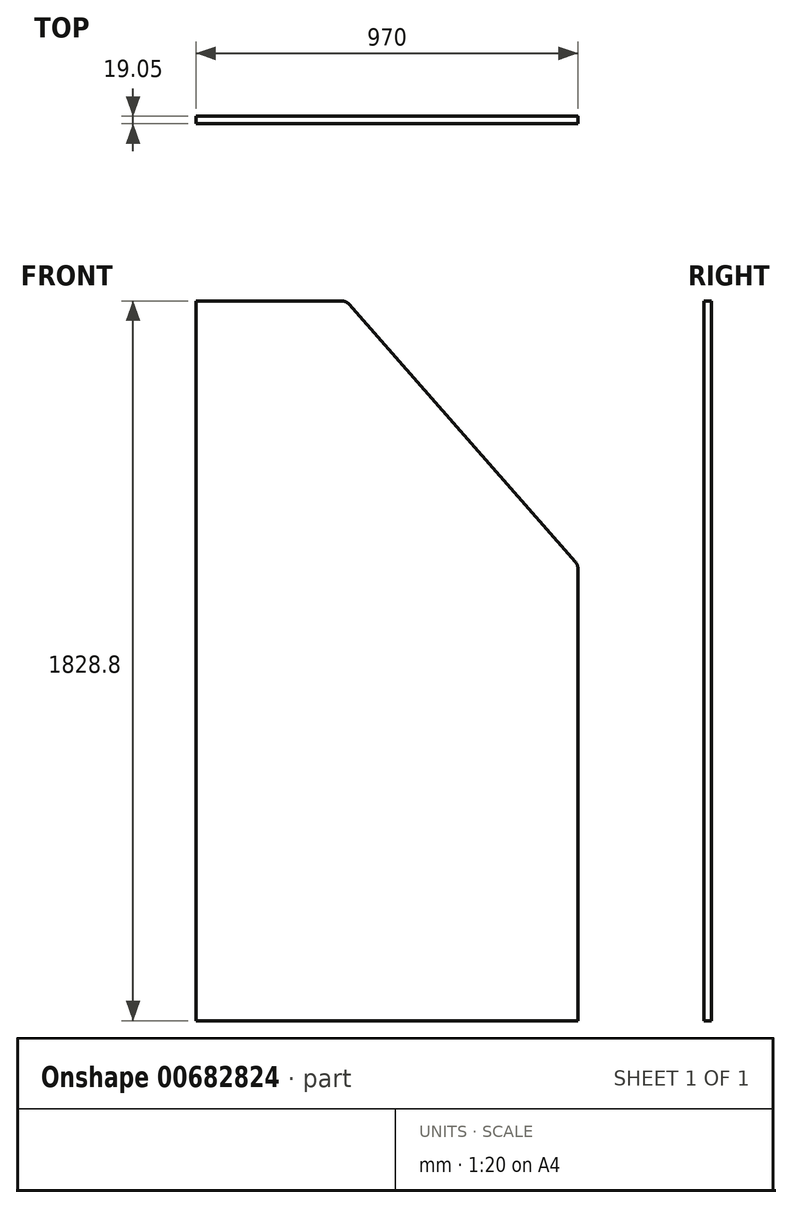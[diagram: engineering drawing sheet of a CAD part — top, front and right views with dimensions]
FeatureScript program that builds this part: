
annotation { "Feature Type Name" : "Feature", "Feature Type Description" : "" }
export const myFeature = defineFeature(function(context is Context, id is Id, definition is map)
    precondition{}
    {
        {
            var Q0;
            Q0=qCreatedBy(makeId("Front.planeOp"),FACE);
            var sketch = newSketch(context, id + "F0", { "sketchPlane" : qUnion([Q0])});
            skLineSegment(sketch, "E0.bottom", {"start": v(0, 0) * mm, "end": v(-970, 0) * mm});
            skLineSegment(sketch, "E0.left", {"start": v(0, 0) * mm, "end": v(0, 1158.24) * mm});
            skLineSegment(sketch, "E0.right", {"start": v(-970, 0) * mm, "end": v(-970, 1828.8) * mm});
            skLineSegment(sketch, "E1", {"start": v(-589, 1828.8) * mm, "end": v(0, 1158.24) * mm});
            skLineSegment(sketch, "E2", {"start": v(-970, 1117.6) * mm, "end": v(-589, 1117.6) * mm, "construction": true});
            skLineSegment(sketch, "E3", {"start": v(-589, 1117.6) * mm, "end": v(-589, 894.08) * mm, "construction": true});
            skLineSegment(sketch, "E4", {"start": v(-589, 894.08) * mm, "end": v(-392.67, 894.08) * mm, "construction": true});
            skLineSegment(sketch, "E5", {"start": v(-392.67, 894.08) * mm, "end": v(-392.67, 670.56) * mm, "construction": true});
            skLineSegment(sketch, "E6", {"start": v(-392.67, 670.56) * mm, "end": v(-196.33, 670.56) * mm, "construction": true});
            skLineSegment(sketch, "E7", {"start": v(-196.33, 670.56) * mm, "end": v(-196.33, 447.04) * mm, "construction": true});
            skLineSegment(sketch, "E8", {"start": v(-196.33, 447.04) * mm, "end": v(0, 447.04) * mm, "construction": true});
            skLineSegment(sketch, "E9", {"start": v(0, 223.52) * mm, "end": v(196.33, 223.52) * mm, "construction": true});
            skLineSegment(sketch, "E10", {"start": v(196.33, 223.52) * mm, "end": v(196.33, 0) * mm, "construction": true});
            skLineSegment(sketch, "E11", {"start": v(-98.17, 447.04) * mm, "end": v(-98.17, 223.52) * mm, "construction": true});
            skLineSegment(sketch, "E12", {"start": v(-98.17, 223.52) * mm, "end": v(0, 223.52) * mm, "construction": true});
            skLineSegment(sketch, "E13", {"start": v(-589, 1117.6) * mm, "end": v(-392.67, 894.08) * mm, "construction": true});
            skLineSegment(sketch, "E14", {"start": v(-589, 1828.8) * mm, "end": v(-970, 1828.8) * mm});
            skLineSegment(sketch, "E15", {"start": v(-196.33, 428) * mm, "end": v(0, 428) * mm, "construction": true});
            skSolve(sketch);
        }
        {
            var Q0;
            Q0=qSketchRegion(id+"F0",true);
            extrude(context, id + "F1", {"entities" : qUnion([Q0]), "depth" : 19.05 * mm, "offsetDistance" : 25.4 * mm});
        }
        {
            var Q0;
            Q0=makeQuery(id+"F1.opExtrude","SWEPT_EDGE",EDGE,{"disambiguationData":[OSD([sQuery(id+"F0.wireOp",EDGE,"E1"),sQuery(id+"F0.wireOp",EDGE,"E14")])]});
            var Q1;
            Q1=makeQuery(id+"F1.opExtrude","SWEPT_EDGE",EDGE,{"disambiguationData":[OSD([sQuery(id+"F0.wireOp",EDGE,"E0.left"),sQuery(id+"F0.wireOp",EDGE,"E1")])]});
            fillet(context, id + "F2", {"entities" : qUnion([Q0, Q1]), "radius" : 25.4 * mm, "tangentPropagation" : true, "allowEdgeOverflow" : false});
        }
    });
